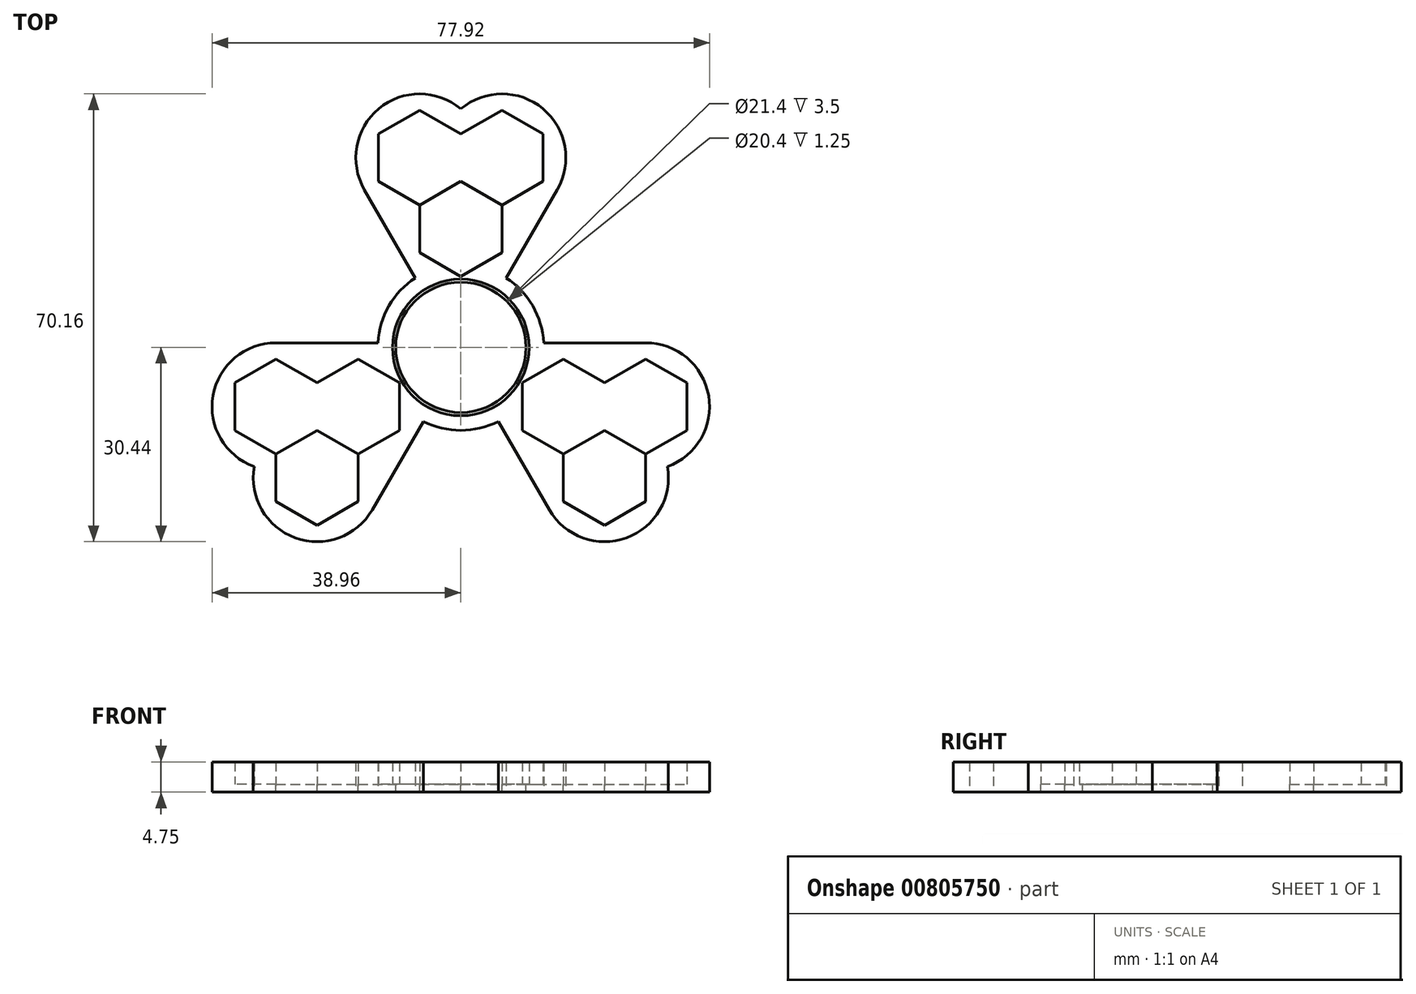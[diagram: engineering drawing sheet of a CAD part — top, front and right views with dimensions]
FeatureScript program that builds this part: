
annotation { "Feature Type Name" : "Feature", "Feature Type Description" : "" }
export const myFeature = defineFeature(function(context is Context, id is Id, definition is map)
    precondition{}
    {
        {
            var Q0;
            Q0=qCreatedBy(makeId("Top.planeOp"),FACE);
            var sketch = newSketch(context, id + "F0", { "sketchPlane" : qUnion([Q0])});
            skCircle(sketch, "E0.cCircle", {"center": v(0, 0) * mm, "radius": 13 * mm, "construction": true});
            skPoint(sketch, "E0.0.midPoint", {"position": v(0, -13) * mm});
            skCircle(sketch, "E1", {"center": v(0, 0) * mm, "radius": 10.7 * mm});
            skCircle(sketch, "E2", {"center": v(0, 0) * mm, "radius": 10.2 * mm});
            skLineSegment(sketch, "E3", {"start": v(0, 0) * mm, "end": v(-22.52, -13) * mm, "construction": true});
            skLineSegment(sketch, "E4", {"start": v(-22.52, -13) * mm, "end": v(-37.36, -21.57) * mm, "construction": true});
            skLineSegment(sketch, "E5", {"start": v(0, 0) * mm, "end": v(22.52, -13) * mm, "construction": true});
            skLineSegment(sketch, "E6", {"start": v(22.52, -13) * mm, "end": v(39.8, -22.98) * mm, "construction": true});
            skLineSegment(sketch, "E7", {"start": v(0, 0) * mm, "end": v(0, 26) * mm, "construction": true});
            skLineSegment(sketch, "E8", {"start": v(0, 26) * mm, "end": v(0, 56) * mm, "construction": true});
            skCircle(sketch, "E9.cCircle", {"center": v(-28.96, -9.28) * mm, "radius": 6.45 * mm, "construction": true});
            skLineSegment(sketch, "E9.0", {"start": v(-22.52, -13) * mm, "end": v(-28.96, -16.72) * mm});
            skLineSegment(sketch, "E9.1", {"start": v(-28.96, -16.72) * mm, "end": v(-35.4, -13) * mm});
            skLineSegment(sketch, "E9.2", {"start": v(-35.4, -13) * mm, "end": v(-35.4, -5.56) * mm});
            skLineSegment(sketch, "E9.3", {"start": v(-35.4, -5.56) * mm, "end": v(-28.96, -1.84) * mm});
            skLineSegment(sketch, "E9.4", {"start": v(-28.96, -1.84) * mm, "end": v(-22.52, -5.56) * mm});
            skLineSegment(sketch, "E9.5", {"start": v(-22.52, -5.56) * mm, "end": v(-22.52, -13) * mm});
            skPoint(sketch, "E9.0.midPoint", {"position": v(-25.74, -14.86) * mm});
            skCircle(sketch, "E10.cCircle", {"center": v(-22.52, -20.44) * mm, "radius": 6.44 * mm, "construction": true});
            skLineSegment(sketch, "E10.0", {"start": v(-28.96, -16.72) * mm, "end": v(-22.52, -13) * mm});
            skLineSegment(sketch, "E10.1", {"start": v(-22.52, -13) * mm, "end": v(-16.07, -16.72) * mm});
            skLineSegment(sketch, "E10.2", {"start": v(-16.07, -16.72) * mm, "end": v(-16.07, -24.16) * mm});
            skLineSegment(sketch, "E10.3", {"start": v(-16.07, -24.16) * mm, "end": v(-22.52, -27.88) * mm});
            skLineSegment(sketch, "E10.4", {"start": v(-22.52, -27.88) * mm, "end": v(-28.96, -24.16) * mm});
            skLineSegment(sketch, "E10.5", {"start": v(-28.96, -24.16) * mm, "end": v(-28.96, -16.72) * mm});
            skCircle(sketch, "E11.cCircle", {"center": v(28.96, -9.28) * mm, "radius": 6.45 * mm, "construction": true});
            skLineSegment(sketch, "E11.0", {"start": v(28.96, -16.72) * mm, "end": v(22.52, -13) * mm});
            skLineSegment(sketch, "E11.1", {"start": v(22.52, -13) * mm, "end": v(22.52, -5.56) * mm});
            skLineSegment(sketch, "E11.2", {"start": v(22.52, -5.56) * mm, "end": v(28.96, -1.84) * mm});
            skLineSegment(sketch, "E11.3", {"start": v(28.96, -1.84) * mm, "end": v(35.4, -5.56) * mm});
            skLineSegment(sketch, "E11.4", {"start": v(35.4, -5.56) * mm, "end": v(35.4, -13) * mm});
            skLineSegment(sketch, "E11.5", {"start": v(35.4, -13) * mm, "end": v(28.96, -16.72) * mm});
            skPoint(sketch, "E11.0.midPoint", {"position": v(25.74, -14.86) * mm});
            skCircle(sketch, "E12.cCircle", {"center": v(22.52, -20.44) * mm, "radius": 6.44 * mm, "construction": true});
            skLineSegment(sketch, "E12.0", {"start": v(22.52, -13) * mm, "end": v(28.96, -16.72) * mm});
            skLineSegment(sketch, "E12.1", {"start": v(28.96, -16.72) * mm, "end": v(28.96, -24.16) * mm});
            skLineSegment(sketch, "E12.2", {"start": v(28.96, -24.16) * mm, "end": v(22.52, -27.88) * mm});
            skLineSegment(sketch, "E12.3", {"start": v(22.52, -27.88) * mm, "end": v(16.07, -24.16) * mm});
            skLineSegment(sketch, "E12.4", {"start": v(16.07, -24.16) * mm, "end": v(16.07, -16.72) * mm});
            skLineSegment(sketch, "E12.5", {"start": v(16.07, -16.72) * mm, "end": v(22.52, -13) * mm});
            skCircle(sketch, "E13.cCircle", {"center": v(-6.45, 29.72) * mm, "radius": 6.44 * mm, "construction": true});
            skLineSegment(sketch, "E13.0", {"start": v(0, 33.44) * mm, "end": v(0, 26) * mm});
            skLineSegment(sketch, "E13.1", {"start": v(0, 26) * mm, "end": v(-6.45, 22.28) * mm});
            skLineSegment(sketch, "E13.2", {"start": v(-6.44, 22.28) * mm, "end": v(-12.9, 26) * mm});
            skLineSegment(sketch, "E13.3", {"start": v(-12.9, 26) * mm, "end": v(-12.9, 33.44) * mm});
            skLineSegment(sketch, "E13.4", {"start": v(-12.9, 33.44) * mm, "end": v(-6.44, 37.16) * mm});
            skLineSegment(sketch, "E13.5", {"start": v(-6.45, 37.16) * mm, "end": v(0, 33.44) * mm});
            skPoint(sketch, "E13.0.midPoint", {"position": v(0, 29.72) * mm});
            skCircle(sketch, "E14.cCircle", {"center": v(6.44, 29.72) * mm, "radius": 6.45 * mm, "construction": true});
            skLineSegment(sketch, "E14.0", {"start": v(0, 33.44) * mm, "end": v(6.44, 37.16) * mm});
            skLineSegment(sketch, "E14.1", {"start": v(6.45, 37.16) * mm, "end": v(12.89, 33.44) * mm});
            skLineSegment(sketch, "E14.2", {"start": v(12.9, 33.44) * mm, "end": v(12.9, 26) * mm});
            skLineSegment(sketch, "E14.3", {"start": v(12.89, 26) * mm, "end": v(6.45, 22.28) * mm});
            skLineSegment(sketch, "E14.4", {"start": v(6.44, 22.28) * mm, "end": v(0, 26) * mm});
            skLineSegment(sketch, "E14.5", {"start": v(0, 26) * mm, "end": v(0, 33.44) * mm});
            skPoint(sketch, "E14.0.midPoint", {"position": v(3.22, 35.3) * mm});
            skCircle(sketch, "E15.cCircle", {"center": v(0, 18.56) * mm, "radius": 6.45 * mm, "construction": true});
            skLineSegment(sketch, "E15.0", {"start": v(0, 26) * mm, "end": v(6.44, 22.28) * mm});
            skLineSegment(sketch, "E15.1", {"start": v(6.45, 22.28) * mm, "end": v(6.45, 14.84) * mm});
            skLineSegment(sketch, "E15.2", {"start": v(6.44, 14.84) * mm, "end": v(0, 11.12) * mm});
            skLineSegment(sketch, "E15.3", {"start": v(0, 11.12) * mm, "end": v(-6.44, 14.84) * mm});
            skLineSegment(sketch, "E15.4", {"start": v(-6.45, 14.84) * mm, "end": v(-6.45, 22.28) * mm});
            skLineSegment(sketch, "E15.5", {"start": v(-6.44, 22.28) * mm, "end": v(0, 26) * mm});
            skPoint(sketch, "E15.0.midPoint", {"position": v(3.22, 24.14) * mm});
            skCircle(sketch, "E16.cCircle", {"center": v(-16.07, -9.28) * mm, "radius": 6.44 * mm, "construction": true});
            skLineSegment(sketch, "E16.0", {"start": v(-9.63, -5.56) * mm, "end": v(-9.63, -13) * mm});
            skLineSegment(sketch, "E16.1", {"start": v(-9.63, -13) * mm, "end": v(-16.07, -16.72) * mm});
            skLineSegment(sketch, "E16.2", {"start": v(-16.07, -16.72) * mm, "end": v(-22.52, -13) * mm});
            skLineSegment(sketch, "E16.3", {"start": v(-22.52, -13) * mm, "end": v(-22.52, -5.56) * mm});
            skLineSegment(sketch, "E16.4", {"start": v(-22.52, -5.56) * mm, "end": v(-16.07, -1.84) * mm});
            skLineSegment(sketch, "E16.5", {"start": v(-16.07, -1.84) * mm, "end": v(-9.63, -5.56) * mm});
            skPoint(sketch, "E16.0.midPoint", {"position": v(-9.63, -9.28) * mm});
            skCircle(sketch, "E17.cCircle", {"center": v(16.07, -9.28) * mm, "radius": 6.45 * mm, "construction": true});
            skLineSegment(sketch, "E17.0", {"start": v(16.07, -1.84) * mm, "end": v(22.52, -5.56) * mm});
            skLineSegment(sketch, "E17.1", {"start": v(22.52, -5.56) * mm, "end": v(22.52, -13) * mm});
            skLineSegment(sketch, "E17.2", {"start": v(22.52, -13) * mm, "end": v(16.07, -16.72) * mm});
            skLineSegment(sketch, "E17.3", {"start": v(16.3, -16.85) * mm, "end": v(16.07, -16.72) * mm});
            skLineSegment(sketch, "E17.4", {"start": v(9.63, -13) * mm, "end": v(9.63, -5.56) * mm});
            skLineSegment(sketch, "E17.5", {"start": v(9.63, -5.56) * mm, "end": v(16.07, -1.84) * mm});
            skPoint(sketch, "E17.0.midPoint", {"position": v(19.3, -3.7) * mm});
            skLineSegment(sketch, "E18", {"start": v(9.63, -13) * mm, "end": v(16.07, -16.72) * mm});
            skArc(sketch, "E19", {"start": v(-2.75, 12.7) * mm, "mid": v(-11.26, 6.5) * mm, "end": v(-12.38, -3.97) * mm});
            skArc(sketch, "E20", {"start": v(-9.63, -8.74) * mm, "mid": v(0, -13) * mm, "end": v(9.63, -8.74) * mm});
            skArc(sketch, "E21", {"start": v(2.75, 12.7) * mm, "mid": v(11.26, 6.5) * mm, "end": v(12.38, -3.97) * mm});
            skCircle(sketch, "E22", {"center": v(-22.52, -20.44) * mm, "radius": 10 * mm, "construction": true});
            skCircle(sketch, "E23", {"center": v(-28.96, -9.28) * mm, "radius": 10 * mm, "construction": true});
            skCircle(sketch, "E24", {"center": v(-6.45, 29.72) * mm, "radius": 10 * mm, "construction": true});
            skCircle(sketch, "E25", {"center": v(6.44, 29.72) * mm, "radius": 10 * mm, "construction": true});
            skCircle(sketch, "E26", {"center": v(28.96, -9.28) * mm, "radius": 10 * mm, "construction": true});
            skCircle(sketch, "E27", {"center": v(22.52, -20.44) * mm, "radius": 10 * mm, "construction": true});
            skLineSegment(sketch, "E28", {"start": v(-6.44, 14.84) * mm, "end": v(-12.9, 26) * mm, "construction": true});
            skLineSegment(sketch, "E29", {"start": v(6.44, 14.84) * mm, "end": v(12.9, 26) * mm, "construction": true});
            skLineSegment(sketch, "E30", {"start": v(16.07, -1.84) * mm, "end": v(28.96, -1.84) * mm, "construction": true});
            skLineSegment(sketch, "E31", {"start": v(9.63, -13) * mm, "end": v(16.07, -24.16) * mm, "construction": true});
            skLineSegment(sketch, "E32", {"start": v(-9.63, -13) * mm, "end": v(-16.07, -24.16) * mm, "construction": true});
            skLineSegment(sketch, "E33", {"start": v(-16.07, -1.84) * mm, "end": v(-28.96, -1.84) * mm, "construction": true});
            skLineSegment(sketch, "E34", {"start": v(-28.96, 0.72) * mm, "end": v(-12.98, 0.72) * mm});
            skLineSegment(sketch, "E35", {"start": v(-13.86, -25.44) * mm, "end": v(-5.87, -11.6) * mm});
            skLineSegment(sketch, "E36", {"start": v(13.86, -25.44) * mm, "end": v(5.87, -11.6) * mm});
            skLineSegment(sketch, "E37", {"start": v(28.96, 0.72) * mm, "end": v(12.98, 0.72) * mm});
            skLineSegment(sketch, "E38", {"start": v(-15.1, 24.72) * mm, "end": v(-7.11, 10.88) * mm});
            skLineSegment(sketch, "E39", {"start": v(15.1, 24.72) * mm, "end": v(7.11, 10.88) * mm});
            skArc(sketch, "E40", {"start": v(-28.96, 0.72) * mm, "mid": v(-38.81, -7.55) * mm, "end": v(-32.36, -18.68) * mm});
            skArc(sketch, "E41", {"start": v(-32.36, -18.68) * mm, "mid": v(-25.95, -29.84) * mm, "end": v(-13.86, -25.44) * mm});
            skArc(sketch, "E42", {"start": v(13.86, -25.44) * mm, "mid": v(25.95, -29.84) * mm, "end": v(32.36, -18.68) * mm});
            skArc(sketch, "E43", {"start": v(32.36, -18.68) * mm, "mid": v(38.81, -7.55) * mm, "end": v(28.96, 0.72) * mm});
            skArc(sketch, "E44", {"start": v(0, 37.37) * mm, "mid": v(-12.86, 37.39) * mm, "end": v(-15.1, 24.72) * mm});
            skArc(sketch, "E45", {"start": v(0, 37.37) * mm, "mid": v(12.86, 37.39) * mm, "end": v(15.1, 24.72) * mm});
            skSolve(sketch);
        }
        {
            var Q0;
            Q0=makeQuery(id+"F0.imprint","IMPRINT",FACE,{"disambiguationData":[TD([[makeQuery(id+"F0.imprint","IMPRINT",EDGE,{"derivedFrom":sQuery(id+"F0.wireOp",EDGE,"E13.2")}),1.0]])]});
            var Q1;
            Q1=makeQuery(id+"F0.imprint","IMPRINT",FACE,{"disambiguationData":[TD([[makeQuery(id+"F0.imprint","IMPRINT",EDGE,{"derivedFrom":sQuery(id+"F0.wireOp",EDGE,"E1")}),-1.0]])]});
            var Q2;
            Q2=makeQuery(id+"F0.imprint","IMPRINT",FACE,{"disambiguationData":[TD([[makeQuery(id+"F0.imprint","IMPRINT",EDGE,{"derivedFrom":sQuery(id+"F0.wireOp",EDGE,"E11.2")}),1.0]])]});
            var Q3;
            Q3=makeQuery(id+"F0.imprint","IMPRINT",FACE,{"disambiguationData":[TD([[makeQuery(id+"F0.imprint","IMPRINT",EDGE,{"derivedFrom":sQuery(id+"F0.wireOp",EDGE,"E9.1")}),1.0]])]});
            extrude(context, id + "F1", {"entities" : qUnion([Q0, Q1, Q2, Q3]), "depth" : 3.5 * mm, "offsetDistance" : 25 * mm});
        }
        {
            var Q0;
            Q0 = qSketchRegion(id + "F0", true);
            var Q1;
            Q1=makeQuery(id+"F0.imprint","IMPRINT",FACE,{"disambiguationData":[TD([[makeQuery(id+"F0.imprint","IMPRINT",EDGE,{"derivedFrom":sQuery(id+"F0.wireOp",EDGE,"E14.0")}),-1.0]])]});
            var Q2;
            Q2=makeQuery(id+"F0.imprint","IMPRINT",FACE,{"disambiguationData":[TD([[makeQuery(id+"F0.imprint","IMPRINT",EDGE,{"derivedFrom":sQuery(id+"F0.wireOp",EDGE,"E13.2")}),-1.0]])]});
            var Q3;
            Q3=makeQuery(id+"F0.imprint","IMPRINT",FACE,{"disambiguationData":[TD([[makeQuery(id+"F0.imprint","IMPRINT",EDGE,{"derivedFrom":sQuery(id+"F0.wireOp",EDGE,"E15.0")}),-1.0]])]});
            var Q4;
            Q4=makeQuery(id+"F0.imprint","IMPRINT",FACE,{"disambiguationData":[TD([[makeQuery(id+"F0.imprint","IMPRINT",EDGE,{"derivedFrom":sQuery(id+"F0.wireOp",EDGE,"E11.2")}),-1.0]])]});
            var Q5;
            {var subQ3=sQuery(id+"F0.wireOp",EDGE,"E17.0");Q5=makeQuery(id+"F0.imprint","IMPRINT",FACE,{"disambiguationData":[TD([[makeQuery(id+"F0.imprint","IMPRINT",EDGE,{"derivedFrom":subQ3}),-1.0]])]});}
            var Q6;
            Q6=makeQuery(id+"F0.imprint","IMPRINT",FACE,{"disambiguationData":[TD([[makeQuery(id+"F0.imprint","IMPRINT",EDGE,{"derivedFrom":sQuery(id+"F0.wireOp",EDGE,"E12.0")}),-1.0]])]});
            var Q7;
            {var subQ0=sQuery(id+"F0.wireOp",EDGE,"E16.1");Q7=makeQuery(id+"F0.imprint","IMPRINT",FACE,{"disambiguationData":[TD([[makeQuery(id+"F0.imprint","IMPRINT",EDGE,{"derivedFrom":subQ0}),-1.0]])]});}
            var Q8;
            Q8=makeQuery(id+"F0.imprint","IMPRINT",FACE,{"disambiguationData":[TD([[makeQuery(id+"F0.imprint","IMPRINT",EDGE,{"derivedFrom":sQuery(id+"F0.wireOp",EDGE,"E9.1")}),-1.0]])]});
            var Q9;
            Q9=makeQuery(id+"F0.imprint","IMPRINT",FACE,{"disambiguationData":[TD([[makeQuery(id+"F0.imprint","IMPRINT",EDGE,{"derivedFrom":sQuery(id+"F0.wireOp",EDGE,"E10.0")}),-1.0]])]});
            var Q10;
            Q10=makeQuery(id+"F0.imprint","IMPRINT",FACE,{"disambiguationData":[TD([[makeQuery(id+"F0.imprint","IMPRINT",EDGE,{"derivedFrom":sQuery(id+"F0.wireOp",EDGE,"E1")}),1.0]])]});
            extrude(context, id + "F2", {"entities" : qUnion([Q0, Q1, Q2, Q3, Q4, Q5, Q6, Q7, Q8, Q9, Q10]), "operationType" : NewBodyOperationType.ADD, "oppositeDirection" : true, "depth" : 1.25 * mm, "offsetDistance" : 25 * mm});
        }
    });
